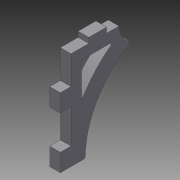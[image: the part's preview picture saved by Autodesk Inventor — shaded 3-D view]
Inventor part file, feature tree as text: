
AUTODESK INVENTOR PART (.ipt)
format: ipt  version: 2015 (Build 190159000, 159)  size: 134,144 bytes
history: native  units: mm
features: extrude x2, fillet x2, sketch x1
ambient origin geometry x8: Origin, YZ Plane, XZ Plane, XY Plane, X Axis, Y Axis, Z Axis, Center Point
bodies: Body1 (feature_tree)
feature tree (5):
  extrude  "Extrusion2"  TaperAngle=60.0deg  [1 undecoded]
  fillet  "Fillet3"  Radius=50.0mm
  extrude  "Extrusion5"  Depth=10.0mm
  fillet  "Fillet7"  Radius=10.0mm
  sketch  "Sketch1"  dims[d0=100.0mm d4=60.0deg d5=60.0deg d6=50.0mm d8=10.0mm d9=10.0mm d10=3.0mm d11=10.0mm d12=6.0mm d13=11.145398mm d14=55.0mm d15=55.0mm d18=10.0mm d23=45.0deg d30=10.0mm d31=6.0mm d32=19.0mm d38=58.0mm d39=6.0mm d40=0.0mm d41=0.75mm d42=6.0mm d43=6.0mm d50=7.0mm d51=16.0mm d57=12.0mm d63=10.0mm d64=0.0mm d68=0.5mm d69=7.0mm d70=7.0mm d73=3.0mm]
note: 1 required parameter value undecoded (feature->parameter linkage not recoverable at this tier; creation-order binding heuristic only, values carry confidence <= 0.55)
